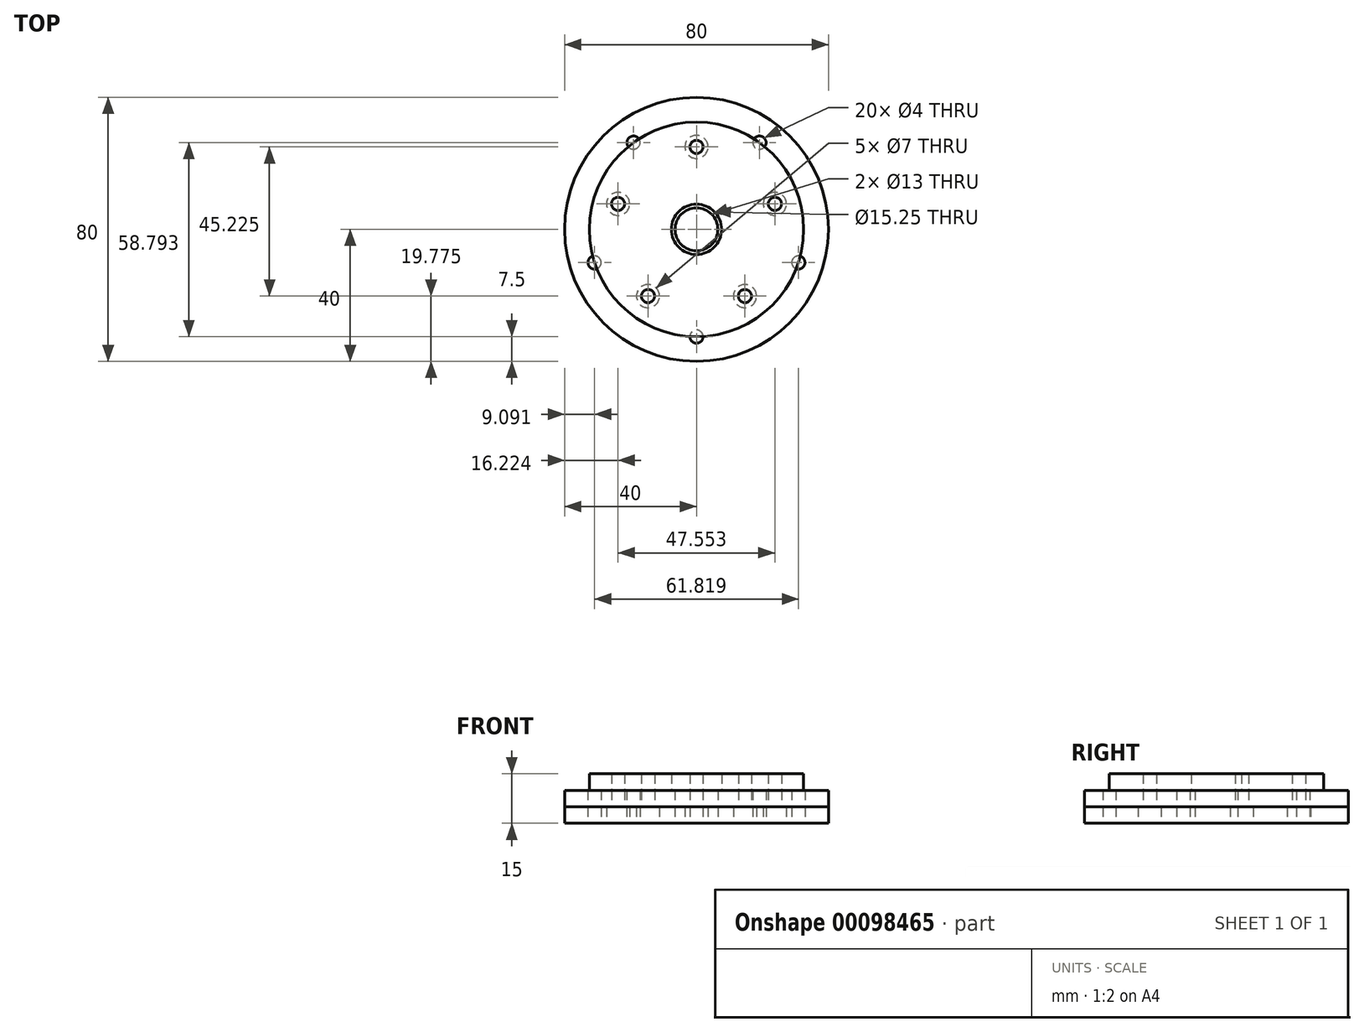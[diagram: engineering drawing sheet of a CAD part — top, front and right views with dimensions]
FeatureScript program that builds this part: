
annotation { "Feature Type Name" : "Feature", "Feature Type Description" : "" }
export const myFeature = defineFeature(function(context is Context, id is Id, definition is map)
    precondition{}
    {
        {
            var Q0;
            Q0=qCreatedBy(makeId("Top.planeOp"),FACE);
            var sketch = newSketch(context, id + "F0", { "sketchPlane" : qUnion([Q0])});
            skCircle(sketch, "E0", {"center": v(0, 0) * mm, "radius": 40 * mm});
            skCircle(sketch, "E1", {"center": v(0, 0) * mm, "radius": 6.5 * mm});
            skCircle(sketch, "E2", {"center": v(0, 0) * mm, "radius": 25 * mm, "construction": true});
            skCircle(sketch, "E3", {"center": v(0, 25) * mm, "radius": 3.5 * mm});
            skCircle(sketch, "E4.1.0", {"center": v(-23.78, 7.73) * mm, "radius": 3.5 * mm});
            skCircle(sketch, "E4.2.0", {"center": v(-14.7, -20.23) * mm, "radius": 3.5 * mm});
            skCircle(sketch, "E4.3.0", {"center": v(14.7, -20.23) * mm, "radius": 3.5 * mm});
            skCircle(sketch, "E4.4.0", {"center": v(23.78, 7.73) * mm, "radius": 3.5 * mm});
            skCircle(sketch, "E5", {"center": v(0, 0) * mm, "radius": 32.5 * mm, "construction": true});
            skCircle(sketch, "E6", {"center": v(19.1, 26.3) * mm, "radius": 2 * mm});
            skLineSegment(sketch, "E7", {"start": v(0, 0) * mm, "end": v(19.1, 26.3) * mm, "construction": true});
            skCircle(sketch, "E8.1.0", {"center": v(-19.1, 26.3) * mm, "radius": 2 * mm});
            skCircle(sketch, "E8.2.0", {"center": v(-30.9, -10.04) * mm, "radius": 2 * mm});
            skCircle(sketch, "E8.3.0", {"center": v(0, -32.5) * mm, "radius": 2 * mm});
            skCircle(sketch, "E8.4.0", {"center": v(30.9, -10.04) * mm, "radius": 2 * mm});
            skSolve(sketch);
        }
        {
            var Q0;
            Q0 = qSketchRegion(id + "F0", true);
            extrude(context, id + "F1", {"entities" : qUnion([Q0]), "depth" : 5 * mm});
        }
        {
            var Q0;
            Q0=makeQuery(id+"F1.opExtrude","CAP_FACE",FACE,{"disambiguationData":[OSD([sQuery(id+"F0.wireOp",EDGE,"E0"),sQuery(id+"F0.wireOp",EDGE,"E1"),sQuery(id+"F0.wireOp",EDGE,"E3"),sQuery(id+"F0.wireOp",EDGE,"E4.1.0"),sQuery(id+"F0.wireOp",EDGE,"E4.2.0"),sQuery(id+"F0.wireOp",EDGE,"E4.3.0"),sQuery(id+"F0.wireOp",EDGE,"E4.4.0"),sQuery(id+"F0.wireOp",EDGE,"E6"),sQuery(id+"F0.wireOp",EDGE,"E8.1.0"),sQuery(id+"F0.wireOp",EDGE,"E8.2.0"),sQuery(id+"F0.wireOp",EDGE,"E8.3.0"),sQuery(id+"F0.wireOp",EDGE,"E8.4.0")])],"isStart":false});
            var sketch = newSketch(context, id + "F2", { "sketchPlane" : qUnion([Q0])});
            skCircle(sketch, "E9.0", {"center": v(0, 0) * mm, "radius": 40 * mm});
            skCircle(sketch, "E9.1", {"center": v(19.1, 26.3) * mm, "radius": 2 * mm});
            skCircle(sketch, "E9.2", {"center": v(-19.1, 26.3) * mm, "radius": 2 * mm});
            skCircle(sketch, "E9.3", {"center": v(-30.9, -10.04) * mm, "radius": 2 * mm});
            skCircle(sketch, "E9.4", {"center": v(0, -32.5) * mm, "radius": 2 * mm});
            skCircle(sketch, "E9.5", {"center": v(30.9, -10.04) * mm, "radius": 2 * mm});
            skCircle(sketch, "E9.6", {"center": v(0, 0) * mm, "radius": 6.5 * mm});
            skCircle(sketch, "E10", {"center": v(0, 25) * mm, "radius": 2 * mm});
            skCircle(sketch, "E11.1.0", {"center": v(-23.78, 7.73) * mm, "radius": 2 * mm});
            skCircle(sketch, "E11.2.0", {"center": v(-14.7, -20.23) * mm, "radius": 2 * mm});
            skCircle(sketch, "E11.3.0", {"center": v(14.7, -20.23) * mm, "radius": 2 * mm});
            skCircle(sketch, "E11.4.0", {"center": v(23.78, 7.73) * mm, "radius": 2 * mm});
            skSolve(sketch);
        }
        {
            var Q0;
            Q0 = qSketchRegion(id + "F2", true);
            extrude(context, id + "F3", {"entities" : qUnion([Q0]), "depth" : 5 * mm});
        }
        {
            var Q0;
            Q0=makeQuery(id+"F3.opExtrude","CAP_FACE",FACE,{"disambiguationData":[OSD([sQuery(id+"F2.wireOp",EDGE,"E9.0"),sQuery(id+"F2.wireOp",EDGE,"E9.1"),sQuery(id+"F2.wireOp",EDGE,"E9.2"),sQuery(id+"F2.wireOp",EDGE,"E9.3"),sQuery(id+"F2.wireOp",EDGE,"E9.4"),sQuery(id+"F2.wireOp",EDGE,"E9.5"),sQuery(id+"F2.wireOp",EDGE,"E9.6"),sQuery(id+"F2.wireOp",EDGE,"E10"),sQuery(id+"F2.wireOp",EDGE,"E11.1.0"),sQuery(id+"F2.wireOp",EDGE,"E11.2.0"),sQuery(id+"F2.wireOp",EDGE,"E11.3.0"),sQuery(id+"F2.wireOp",EDGE,"E11.4.0")])],"isStart":false});
            var sketch = newSketch(context, id + "F4", { "sketchPlane" : qUnion([Q0])});
            skCircle(sketch, "E12.0", {"center": v(0, 25) * mm, "radius": 2 * mm});
            skCircle(sketch, "E12.1", {"center": v(23.78, 7.73) * mm, "radius": 2 * mm});
            skCircle(sketch, "E12.2", {"center": v(14.7, -20.23) * mm, "radius": 2 * mm});
            skCircle(sketch, "E12.3", {"center": v(-14.7, -20.23) * mm, "radius": 2 * mm});
            skCircle(sketch, "E12.4", {"center": v(-23.78, 7.73) * mm, "radius": 2 * mm});
            skCircle(sketch, "E13", {"center": v(0, 0) * mm, "radius": 7.62 * mm});
            skCircle(sketch, "E14", {"center": v(0, 0) * mm, "radius": 32.5 * mm});
            skSolve(sketch);
        }
        {
            var Q0;
            Q0 = qSketchRegion(id + "F4", true);
            extrude(context, id + "F5", {"entities" : qUnion([Q0]), "depth" : 5 * mm});
        }
    });
